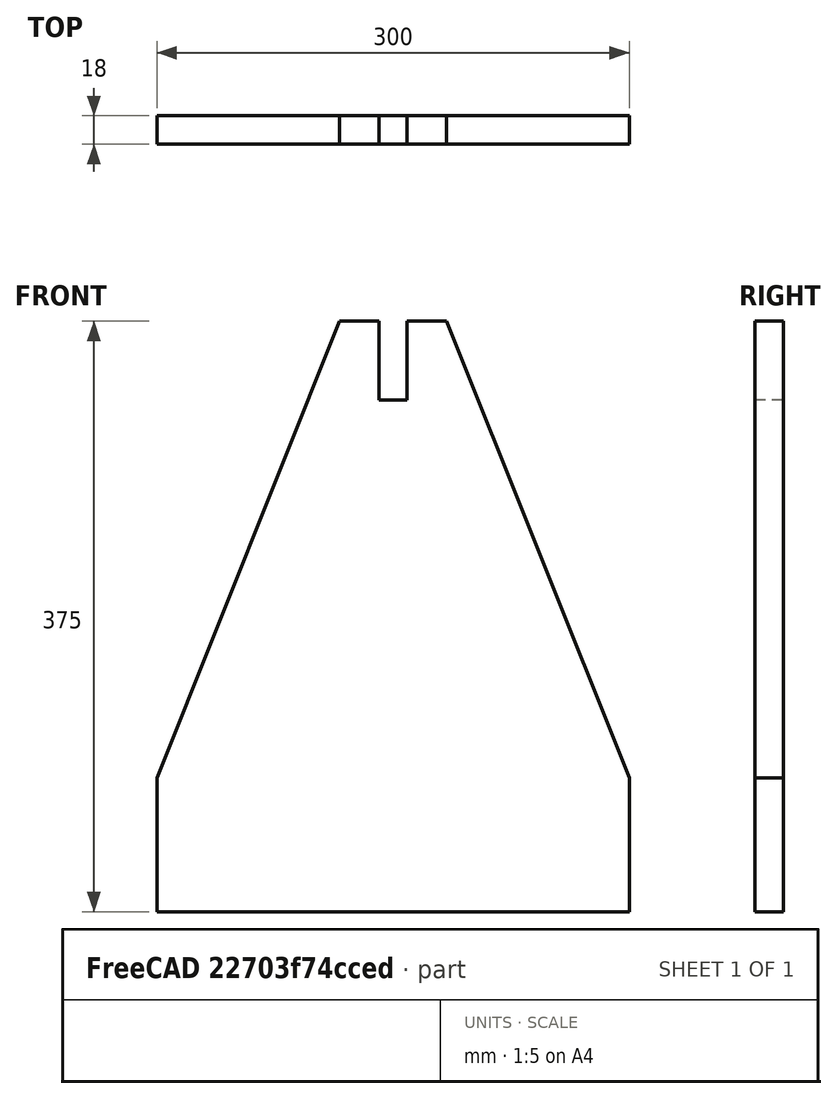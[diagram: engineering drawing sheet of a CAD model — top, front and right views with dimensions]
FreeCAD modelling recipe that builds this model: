
FCSTD DOCUMENT  (FreeCAD 0.20R29177 (Git))
Label: Wood sides Y
License: All rights reserved
LicenseURL: http://en.wikipedia.org/wiki/All_rights_reserved
objects: Sketcher::SketchObject×1, PartDesign::Pad×1, PartDesign::Body×1
note: 4 computed .brp shape members not serialized (recipe doc carries the construction recipe); baked Part::Feature solids carry a one-line shape summary decoded from their .brp

FEATURE [Sketcher::SketchObject] Sketch
  FullyConstrained = true
  MapMode = 5
  Placement = pos=(0,0,0) rot=(1,0,0;1.5708rad)
  Support = -> [XZ_Plane]
  sketch-geometry (10):
    g0: LineSegment StartX=0 StartY=0 StartZ=0 EndX=0 EndY=85 EndZ=0
    g1: LineSegment StartX=0 StartY=85 StartZ=0 EndX=116 EndY=375 EndZ=0
    g2: LineSegment StartX=184 StartY=375 StartZ=0 EndX=300 EndY=85 EndZ=0
    g3: LineSegment StartX=300 StartY=85 StartZ=0 EndX=300 EndY=0 EndZ=0
    g4: LineSegment StartX=300 StartY=0 StartZ=0 EndX=0 EndY=0 EndZ=0
    g5: LineSegment StartX=116 StartY=375 StartZ=0 EndX=141 EndY=375 EndZ=0
    g6: LineSegment StartX=141 StartY=375 StartZ=0 EndX=141 EndY=325 EndZ=0
    g7: LineSegment StartX=141 StartY=325 StartZ=0 EndX=159 EndY=325 EndZ=0
    g8: LineSegment StartX=159 StartY=325 StartZ=0 EndX=159 EndY=375 EndZ=0
    g9: LineSegment StartX=159 StartY=375 StartZ=0 EndX=184 EndY=375 EndZ=0
  constraints (30):
    c: Coincident(g1,g0)
    c: Coincident(g3,g2)
    c: Coincident(g4,g3)
    c: Coincident(g4,g0)
    c: Horizontal(g4)
    c: Vertical(g0)
    c: PointOnObject(g-1,g4)
    c: Equal(g0,g3)
    c: Vertical(g3)
    c: Equal(g1,g2)
    c: DistanceY(g0,g0) = 85
    c: PointOnObject(g-1,g0)
    c: DistanceX(g4,g4) = 300
    c: Coincident(g5,g1)
    c: Vertical(g6)
    c: Horizontal(g7)
    c: Coincident(g8,g7)
    c: Vertical(g8)
    c: Horizontal(g5)
    c: PointOnObject(g8,g5)
    c: Coincident(g6,g5)
    c: Coincident(g6,g7)
    c: Coincident(g9,g8)
    c: Coincident(g9,g2)
    c: Horizontal(g9)
    c: Equal(g9,g5)
    c: DistanceX(g5,g5) = 25
    c: DistanceX(g7,g7) = 18
    c: DistanceY(g6,g6) = 50
    c: DistanceY(g3,g2) = 375
FEATURE [PartDesign::Pad] Pad
  Direction = (0,-1,-2e-16)
  Length = 18
  Length2 = 100
  Placement = pos=(0,0,0) rot=(1,0,0;1.5708rad)
  Profile = -> Sketch
  Type = 0
FEATURE [PartDesign::Body] Body
  Group = -> [Sketch,Pad]
  Origin = -> Origin
  Tip = -> Pad
